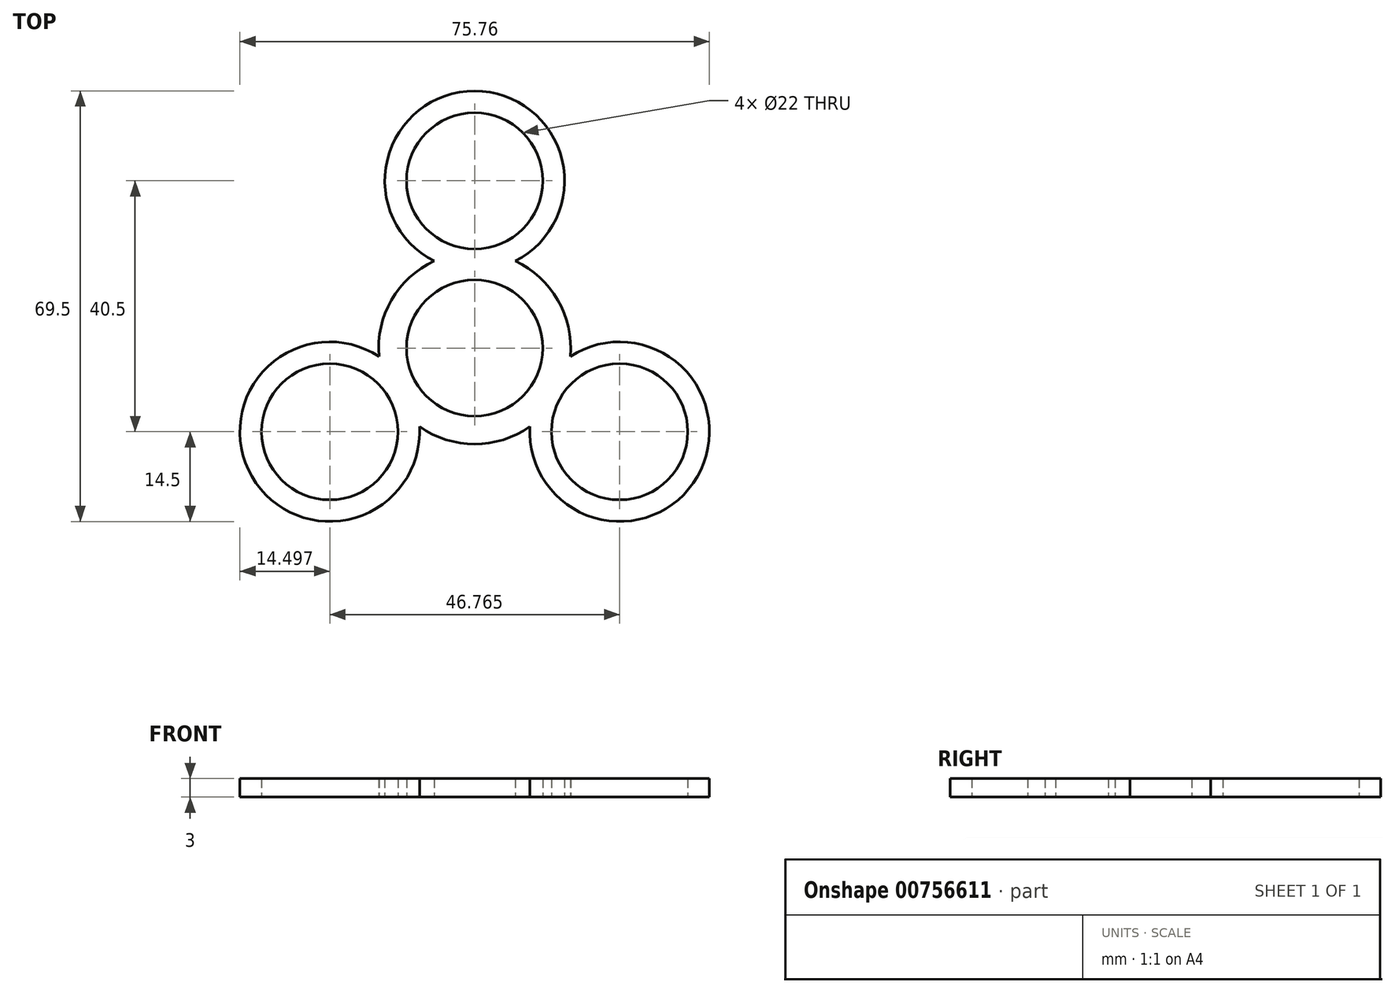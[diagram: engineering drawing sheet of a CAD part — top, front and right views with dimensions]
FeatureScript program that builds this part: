
annotation { "Feature Type Name" : "Feature", "Feature Type Description" : "" }
export const myFeature = defineFeature(function(context is Context, id is Id, definition is map)
    precondition{}
    {
        {
            var Q0;
            Q0=qCreatedBy(makeId("Top.planeOp"),FACE);
            var sketch = newSketch(context, id + "F0", { "sketchPlane" : qUnion([Q0])});
            skCircle(sketch, "E0", {"center": v(0, 0) * mm, "radius": 11 * mm});
            skCircle(sketch, "E1", {"center": v(0, 27) * mm, "radius": 11 * mm});
            skArc(sketch, "E2", {"start": v(-6.53, 14.06) * mm, "mid": v(-13.42, 7.75) * mm, "end": v(-15.44, -1.37) * mm});
            skArc(sketch, "E3", {"start": v(6.53, 14.06) * mm, "mid": v(0, 41.5) * mm, "end": v(-6.53, 14.06) * mm});
            skLineSegment(sketch, "E4.trimOffspring", {"start": v(0, 15.5) * mm, "end": v(0, 16) * mm});
            skCircle(sketch, "E5.1.1", {"center": v(-23.38, -13.5) * mm, "radius": 11 * mm});
            skArc(sketch, "E5.1.2", {"start": v(-15.44, -1.37) * mm, "mid": v(-35.94, -20.75) * mm, "end": v(-8.9, -12.69) * mm});
            skArc(sketch, "E5.1.3", {"start": v(-8.9, -12.69) * mm, "mid": v(0, -15.5) * mm, "end": v(8.9, -12.69) * mm});
            skCircle(sketch, "E5.2.1", {"center": v(23.38, -13.5) * mm, "radius": 11 * mm});
            skArc(sketch, "E5.2.2", {"start": v(8.9, -12.69) * mm, "mid": v(35.94, -20.75) * mm, "end": v(15.44, -1.37) * mm});
            skArc(sketch, "E5.2.3", {"start": v(15.44, -1.37) * mm, "mid": v(13.42, 7.75) * mm, "end": v(6.53, 14.06) * mm});
            skArc(sketch, "E6.trimOffspring", {"start": v(15.44, -1.37) * mm, "mid": v(15.13, 3.35) * mm, "end": v(13.42, 7.75) * mm});
            skSolve(sketch);
        }
        {
            var Q0;
            Q0 = qSketchRegion(id + "F0", true);
            extrude(context, id + "F1", {"entities" : qUnion([Q0]), "depth" : 3 * mm, "offsetDistance" : 25 * mm});
        }
    });
